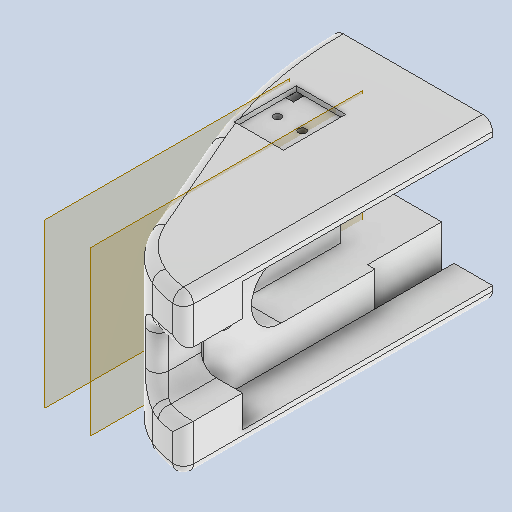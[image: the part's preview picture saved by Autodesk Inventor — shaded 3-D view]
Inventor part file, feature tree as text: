
AUTODESK INVENTOR PART (.ipt)
format: ipt  version: 2025 (Build 290162010, 162A)  size: 390,656 bytes
history: native  units: mm
features: extrude x8, sketch x7, other x4, hole x3, fillet x3, plane x2, reference x2
ambient origin geometry x8: Origin, YZ Plane, XZ Plane, XY Plane, X Axis, Y Axis, Z Axis, Center Point
bodies: Volumenkörper1 (feature_tree)
feature tree (29):
  sketch  "Skizze1"  dims[d0=5.0mm d1=45.0mm d2=30.0mm d3=0.0mm]
  extrude  "Extrusion1"  Depth=30.0mm TaperAngle=0.0deg
  hole  "Bohrung2"  [1 undecoded]
  extrude  "Extrusion2"  [1 undecoded]
  plane  "Arbeitsebene1"
  hole  "Bohrung4"  [1 undecoded]
  extrude  "Extrusion3"  Depth=2.0mm
  plane  "Arbeitsebene2"
  hole  "Bohrung5"  [1 undecoded]
  extrude  "Extrusion4"  Depth=2.0mm
  extrude  "Extrusion5"  Depth=2.0mm TaperAngle=0.0deg
  extrude  "Extrusion6"  [1 undecoded]
  fillet  "Rundung2"  Radius=7.8mm
  sketch  "Skizze13"  dims[d41=12.0mm d42=0.0mm d43=0.0mm d44=3.2mm d45=6.0mm d46=6.3mm d47=2.0mm d48=90.0deg d49=8.0mm d50=20.594885mm d51=12.0mm d52=8.0mm d53=0.0mm d54=-19.5mm d56=7.8mm d57=1.0mm d58=0.0mm d59=2.0mm d60=0.0mm d61=12.0mm d62=8.5mm d63=0.0mm d65=0.5mm d66=3.0mm d67=1.0mm d68=0.0mm d69=8.5mm d70=0.0mm d71=3.0mm d72=15.0mm d73=15.0mm d75=35.0mm d76=2.0mm d77=0.0mm d78=2.0mm]
  extrude  "Extrusion7"  Depth=2.0mm TaperAngle=0.0deg
  extrude  "Extrusion8"  Depth=2.0mm TaperAngle=0.0deg
  fillet  "Rundung3"  Radius=12.0mm
  fillet  "Rundung4"  Radius=8.5mm
  reference  "Referenz1"
  sketch  "Skizze3"  dims[d4=15.0mm d14=6.5mm]
  reference  "Referenz3"
  sketch  "Skizze5"  dims[d15=5.0mm]
  sketch  "Skizze7"  dims[d16=1.567mm d17=8.0mm d18=4.0mm d19=2.0mm d20=90.0deg d21=10.0mm d22=20.594885mm d30=-10.0mm]
  sketch  "Skizze8"  dims[d31=15.0mm d32=15.0mm]
  sketch  "Skizze9"  dims[d33=3.2mm d34=6.0mm d35=6.3mm d36=2.0mm d37=90.0deg d38=8.0mm d39=20.594885mm d40=14.0mm]
  other  "<userpath>\GIT\HDVKBM\CAD\Krandemonstrator\Demonstrator.iam"
  other  "Demonstrator.iam"
  other  "Träger:1"
  other  "AS 1112 (2) - Metrisch M4  Typ 5:1"
note: 5 required parameter values undecoded (feature->parameter linkage not recoverable at this tier; creation-order binding heuristic only, values carry confidence <= 0.55)
